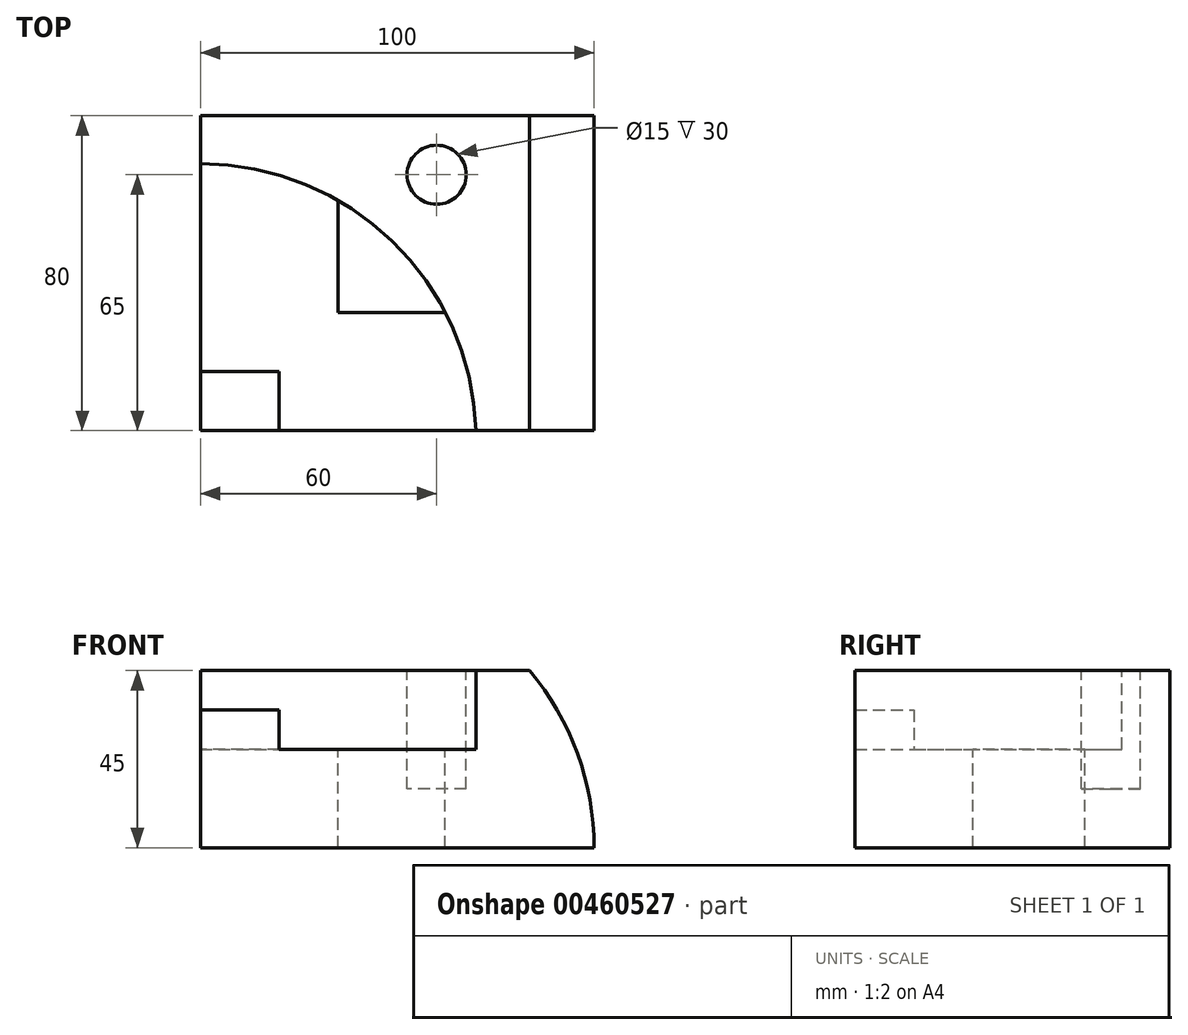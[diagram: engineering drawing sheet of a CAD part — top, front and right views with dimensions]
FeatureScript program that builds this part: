
annotation { "Feature Type Name" : "Feature", "Feature Type Description" : "" }
export const myFeature = defineFeature(function(context is Context, id is Id, definition is map)
    precondition{}
    {
        {
            var Q0;
            Q0=qCreatedBy(makeId("Top.planeOp"),FACE);
            var sketch = newSketch(context, id + "F0", { "sketchPlane" : qUnion([Q0])});
            skLineSegment(sketch, "E0.bottom", {"start": v(0, 0) * mm, "end": v(100, 0) * mm});
            skLineSegment(sketch, "E0.top", {"start": v(0, 80) * mm, "end": v(100, 80) * mm});
            skLineSegment(sketch, "E0.left", {"start": v(0, 0) * mm, "end": v(0, 80) * mm});
            skLineSegment(sketch, "E0.right", {"start": v(100, 0) * mm, "end": v(100, 80) * mm});
            skSolve(sketch);
        }
        {
            var Q0;
            Q0 = qSketchRegion(id + "F0", true);
            extrude(context, id + "F1", {"entities" : qUnion([Q0]), "depth" : 45 * mm});
        }
        {
            var Q0;
            Q0=makeQuery(id+"F1.opExtrude","CAP_FACE",FACE,{"disambiguationData":[OSD([sQuery(id+"F0.wireOp",EDGE,"E0.bottom"),sQuery(id+"F0.wireOp",EDGE,"E0.top"),sQuery(id+"F0.wireOp",EDGE,"E0.left"),sQuery(id+"F0.wireOp",EDGE,"E0.right")])],"isStart":false});
            var sketch = newSketch(context, id + "F2", { "sketchPlane" : qUnion([Q0])});
            skCircle(sketch, "E1", {"center": v(0, -2.16) * mm, "radius": 70 * mm});
            skSolve(sketch);
        }
        {
            var Q0;
            Q0 = qSketchRegion(id + "F2", true);
            extrude(context, id + "F3", {"entities" : qUnion([Q0]), "operationType" : NewBodyOperationType.REMOVE, "oppositeDirection" : true, "depth" : 20 * mm});
        }
        {
            var Q0;
            Q0=makeQuery(id+"F3.boolean.opBoolean","COPY",FACE,{"derivedFrom":makeQuery(id+"F3.opExtrude","CAP_FACE",FACE,{"disambiguationData":[OSD([sQuery(id+"F2.wireOp",EDGE,"E1")])],"isStart":false})});
            var sketch = newSketch(context, id + "F4", { "sketchPlane" : qUnion([Q0])});
            skLineSegment(sketch, "E2.bottom", {"start": v(0, 0) * mm, "end": v(20, 0) * mm});
            skLineSegment(sketch, "E2.top", {"start": v(0, 15) * mm, "end": v(20, 15) * mm});
            skLineSegment(sketch, "E2.left", {"start": v(0, 0) * mm, "end": v(0, 15) * mm});
            skLineSegment(sketch, "E2.right", {"start": v(20, 0) * mm, "end": v(20, 15) * mm});
            skSolve(sketch);
        }
        {
            var Q0;
            Q0 = qSketchRegion(id + "F4", true);
            extrude(context, id + "F5", {"entities" : qUnion([Q0]), "operationType" : NewBodyOperationType.ADD, "depth" : 10 * mm});
        }
        {
            var Q0;
            Q0=makeQuery(id+"F3.boolean.opBoolean","COPY",FACE,{"derivedFrom":makeQuery(id+"F3.opExtrude","CAP_FACE",FACE,{"disambiguationData":[OSD([sQuery(id+"F2.wireOp",EDGE,"E1")])],"isStart":false})});
            var sketch = newSketch(context, id + "F6", { "sketchPlane" : qUnion([Q0])});
            skLineSegment(sketch, "E3", {"start": v(35, 58.46) * mm, "end": v(35, 30) * mm});
            skLineSegment(sketch, "E4", {"start": v(35, 30) * mm, "end": v(62.18, 30) * mm});
            skSolve(sketch);
        }
        {
            var Q0;
            {var subQ0=sQuery(id+"F6.wireOp",EDGE,"E3");Q0=makeQuery(id+"F6.imprint","IMPRINT",FACE,{"disambiguationData":[TD([[makeQuery(id+"F6.imprint","IMPRINT",EDGE,{"derivedFrom":subQ0}),1.0]])]});}
            extrude(context, id + "F7", {"entities" : qUnion([Q0]), "operationType" : NewBodyOperationType.REMOVE, "endBound" : BoundingType.UP_TO_NEXT, "oppositeDirection" : true, "depth" : 25 * mm});
        }
        {
            var Q0;
            Q0=makeQuery(id+"F1.opExtrude","CAP_FACE",FACE,{"disambiguationData":[OSD([sQuery(id+"F0.wireOp",EDGE,"E0.bottom"),sQuery(id+"F0.wireOp",EDGE,"E0.top"),sQuery(id+"F0.wireOp",EDGE,"E0.left"),sQuery(id+"F0.wireOp",EDGE,"E0.right")])],"isStart":false});
            var sketch = newSketch(context, id + "F8", { "sketchPlane" : qUnion([Q0])});
            skCircle(sketch, "E5", {"center": v(60, 65) * mm, "radius": 7.5 * mm});
            skSolve(sketch);
        }
        {
            var Q0;
            Q0 = qSketchRegion(id + "F8", true);
            extrude(context, id + "F9", {"entities" : qUnion([Q0]), "operationType" : NewBodyOperationType.REMOVE, "oppositeDirection" : true, "depth" : 30 * mm});
        }
        {
            var Q0;
            Q0=makeQuery(id+"F5.boolean.opBoolean","MERGE",FACE,{"derivedFrom":[makeQuery(id+"F1.opExtrude","SWEPT_FACE",FACE,{"disambiguationData":[OSD([sQuery(id+"F0.wireOp",EDGE,"E0.bottom")])]}),makeQuery(id+"F5.opExtrude","SWEPT_FACE",FACE,{"disambiguationData":[OSD([sQuery(id+"F4.wireOp",EDGE,"E2.bottom")])]})]});
            var sketch = newSketch(context, id + "F10", { "sketchPlane" : qUnion([Q0])});
            skLineSegment(sketch, "E6", {"start": v(100, 0) * mm, "end": v(30, 0) * mm});
            skCircle(sketch, "E7", {"center": v(30, 0) * mm, "radius": 70 * mm});
            skSolve(sketch);
        }
        {
            var Q0;
            {var subQ1=sQuery(id+"F0.wireOp",EDGE,"E0.bottom");var subQ2=makeQuery(id+"F1.opExtrude","SWEPT_EDGE",EDGE,{"disambiguationData":[OSD([subQ1,sQuery(id+"F0.wireOp",EDGE,"E0.right")])]});Q0=makeQuery(id+"F10.imprint","IMPRINT",FACE,{"disambiguationData":[TD([[makeQuery(id+"F10.imprint","IMPRINT",EDGE,{"derivedFrom":subQ2}),-1.0]])]});}
            extrude(context, id + "F11", {"entities" : qUnion([Q0]), "operationType" : NewBodyOperationType.REMOVE, "endBound" : BoundingType.UP_TO_NEXT, "oppositeDirection" : true, "depth" : 25 * mm});
        }
    });
